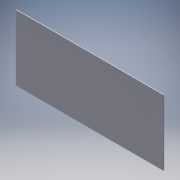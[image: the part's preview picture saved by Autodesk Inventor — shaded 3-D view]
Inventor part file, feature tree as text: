
AUTODESK INVENTOR PART (.ipt)
format: ipt  version: 2019 (Build 230136000, 136)  size: 96,256 bytes
history: native  units: mm
features: extrude x1, sketch x1
ambient origin geometry x8: Origin, YZ Plane, XZ Plane, XY Plane, X Axis, Y Axis, Z Axis, Center Point
bodies: Solid1 (feature_tree)
feature tree (2):
  extrude  "Extrusion1"  Depth=800.0mm
  sketch  "Sketch1"  dims[d0=1800.0mm d1=800.0mm d2=10.0mm d3=0.0mm]
